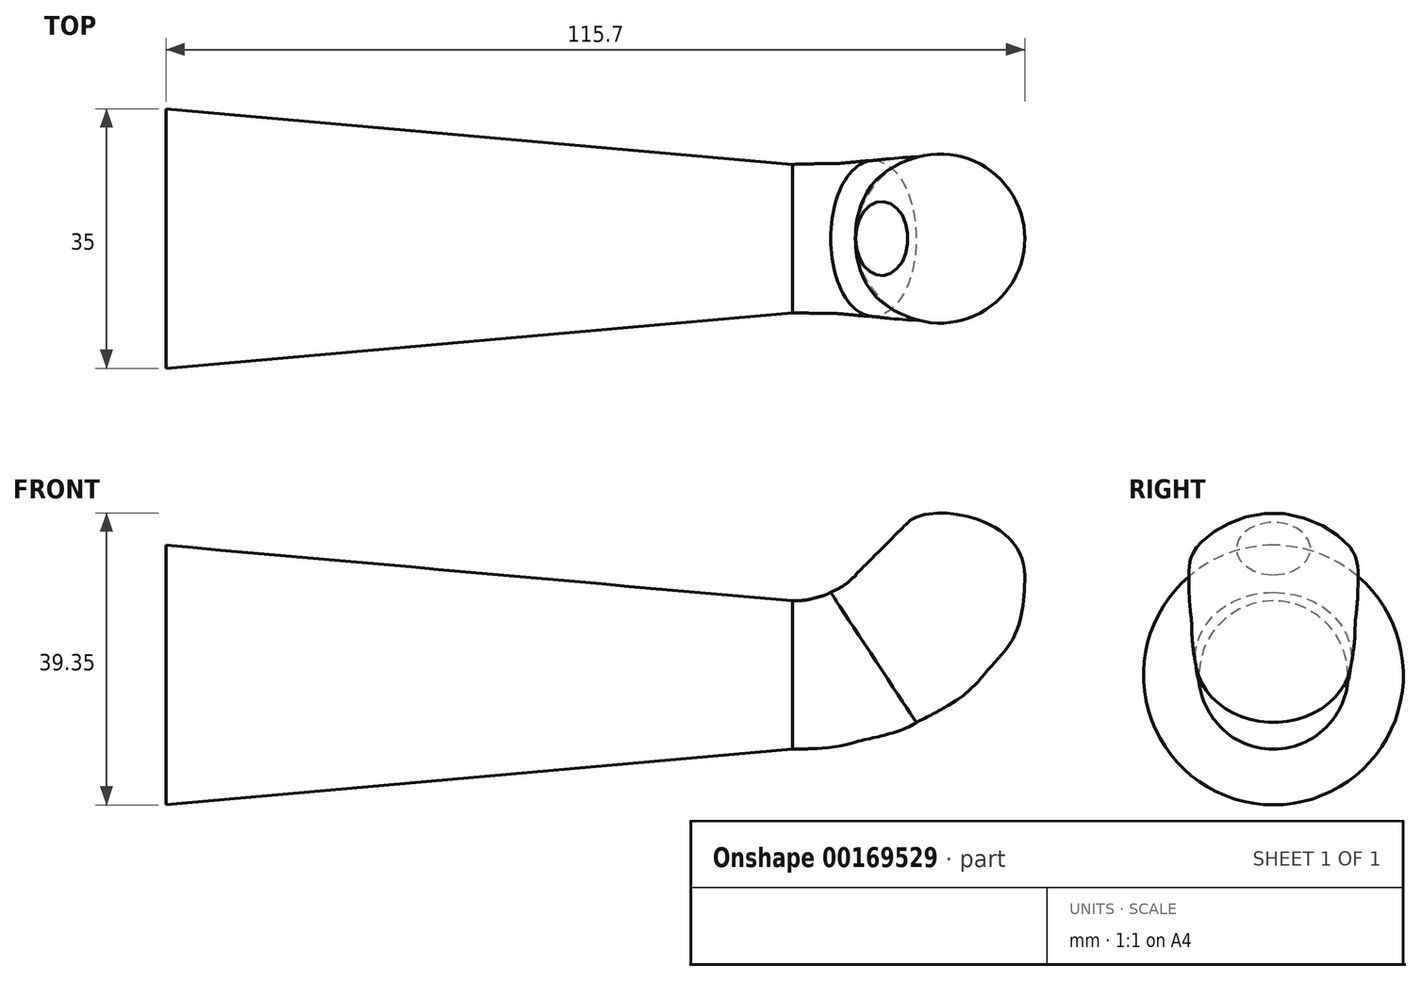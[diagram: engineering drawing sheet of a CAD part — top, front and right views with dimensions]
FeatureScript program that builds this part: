
annotation { "Feature Type Name" : "Feature", "Feature Type Description" : "" }
export const myFeature = defineFeature(function(context is Context, id is Id, definition is map)
    precondition{}
    {
        {
            var Q0;
            Q0=qCreatedBy(makeId("Front.planeOp"),FACE);
            var sketch = newSketch(context, id + "F0", { "sketchPlane" : qUnion([Q0])});
            skLineSegment(sketch, "E0", {"start": v(-55.96, 50) * mm, "end": v(-55.96, -50) * mm});
            skLineSegment(sketch, "E1", {"start": v(36.94, 32.9) * mm, "end": v(47.57, 43.54) * mm});
            skPoint(sketch, "E2", {"position": v(40.5, 36.46) * mm});
            skLineSegment(sketch, "E3", {"start": v(36.96, 32.93) * mm, "end": v(44.04, 40) * mm});
            skPoint(sketch, "E4", {"position": v(-55.96, 9.48) * mm});
            skLineSegment(sketch, "E5", {"start": v(28.46, 29.4) * mm, "end": v(-55.96, 29.4) * mm});
            skPoint(sketch, "E6.visualSharp", {"position": v(33.43, 29.4) * mm});
            skArc(sketch, "E6.filletArc", {"start": v(28.46, 29.4) * mm, "mid": v(33.05, 30.3) * mm, "end": v(36.94, 32.9) * mm});
            skLineSegment(sketch, "E7", {"start": v(28.46, 29.4) * mm, "end": v(28.46, 0) * mm});
            skLineSegment(sketch, "E8", {"start": v(28.46, 21.9) * mm, "end": v(-55.96, 21.9) * mm});
            skSolve(sketch);
        }
        {
            var Q0;
            Q0=sQuery(id+"F0.wireOp",EDGE,"E1");
            extrude(context, id + "F1", {"bodyType" : ToolBodyType.SURFACE, "surfaceEntities" : qUnion([Q0]), "endBound" : BoundingType.SYMMETRIC, "depth" : 15 * mm});
        }
        {
            var Q0;
            Q0=makeQuery(id+"F1.opExtrude","SWEPT_FACE",FACE,{"disambiguationData":[OSD([sQuery(id+"F0.wireOp",EDGE,"E1")])]});
            var sketch = newSketch(context, id + "F2", { "sketchPlane" : qUnion([Q0])});
            skCircle(sketch, "E9", {"center": v(0, 54.4) * mm, "radius": 5 * mm});
            skSolve(sketch);
        }
        {
            var Q0;
            Q0=qCreatedBy(makeId("Front.planeOp"),FACE);
            var sketch = newSketch(context, id + "F3", { "sketchPlane" : qUnion([Q0])});
            skLineSegment(sketch, "E10", {"start": v(28.46, 29.4) * mm, "end": v(28.46, 9.4) * mm});
            skFitSpline(sketch, "E11", {"points": [v(47.48, 43.44) * mm, v(28.46, 9.4) * mm], "startDerivative": vector(67.22, -6.83) * mm, "endDerivative": vector(-97.52, -2.02) * mm});
            skLineSegment(sketch, "E12", {"start": v(36.84, 32.8) * mm, "end": v(59.84, 32.8) * mm});
            skLineSegment(sketch, "E13", {"start": v(36.45, 32.44) * mm, "end": v(53.92, 19.07) * mm});
            skLineSegment(sketch, "E14", {"start": v(33.58, 30.54) * mm, "end": v(45.13, 13) * mm});
            skLineSegment(sketch, "E15", {"start": v(30.98, 29.66) * mm, "end": v(36.61, 10.26) * mm});
            skSolve(sketch);
        }
        {
            var Q0;
            Q0=sQuery(id+"F3.wireOp",EDGE,"E12");
            extrude(context, id + "F4", {"bodyType" : ToolBodyType.SURFACE, "surfaceEntities" : qUnion([Q0]), "endBound" : BoundingType.SYMMETRIC, "depth" : 23 * mm});
        }
        {
            var Q0;
            Q0=sQuery(id+"F3.wireOp",EDGE,"E13");
            extrude(context, id + "F5", {"bodyType" : ToolBodyType.SURFACE, "surfaceEntities" : qUnion([Q0]), "endBound" : BoundingType.SYMMETRIC, "depth" : 22 * mm});
        }
        {
            var Q0;
            Q0=sQuery(id+"F3.wireOp",EDGE,"E14");
            extrude(context, id + "F6", {"bodyType" : ToolBodyType.SURFACE, "surfaceEntities" : qUnion([Q0]), "endBound" : BoundingType.SYMMETRIC, "depth" : 21 * mm});
        }
        {
            var Q0;
            Q0=sQuery(id+"F3.wireOp",EDGE,"E15");
            extrude(context, id + "F7", {"bodyType" : ToolBodyType.SURFACE, "surfaceEntities" : qUnion([Q0]), "endBound" : BoundingType.SYMMETRIC, "depth" : 20.2 * mm});
        }
        {
            var Q0;
            Q0=sQuery(id+"F3.wireOp",EDGE,"E10");
            extrude(context, id + "F8", {"bodyType" : ToolBodyType.SURFACE, "surfaceEntities" : qUnion([Q0]), "endBound" : BoundingType.SYMMETRIC, "depth" : 20 * mm});
        }
        {
            var Q0;
            Q0=makeQuery(id+"F4.opExtrude","SWEPT_FACE",FACE,{"disambiguationData":[OSD([sQuery(id+"F3.wireOp",EDGE,"E12")])]});
            var sketch = newSketch(context, id + "F9", { "sketchPlane" : qUnion([Q0])});
            skPoint(sketch, "E16.centerSnap0", {"position": v(48.34, 11.5) * mm});
            skCircle(sketch, "E17", {"center": v(48.34, 0) * mm, "radius": 11.4 * mm});
            skSolve(sketch);
        }
        {
            var Q0;
            Q0=makeQuery(id+"F5.opExtrude","SWEPT_FACE",FACE,{"disambiguationData":[OSD([sQuery(id+"F3.wireOp",EDGE,"E13")])]});
            var sketch = newSketch(context, id + "F10", { "sketchPlane" : qUnion([Q0])});
            skCircle(sketch, "E18", {"center": v(20.22, 0) * mm, "radius": 11 * mm});
            skPoint(sketch, "E18.centerSnap0", {"position": v(20.22, 11) * mm});
            skSolve(sketch);
        }
        {
            var Q0;
            Q0=makeQuery(id+"F6.opExtrude","SWEPT_FACE",FACE,{"disambiguationData":[OSD([sQuery(id+"F3.wireOp",EDGE,"E14")])]});
            var sketch = newSketch(context, id + "F11", { "sketchPlane" : qUnion([Q0])});
            skCircle(sketch, "E19", {"center": v(0, -3.44) * mm, "radius": 10.5 * mm});
            skPoint(sketch, "E19.centerSnap0", {"position": v(10.5, -3.44) * mm});
            skSolve(sketch);
        }
        {
            var Q0;
            Q0=makeQuery(id+"F7.opExtrude","SWEPT_FACE",FACE,{"disambiguationData":[OSD([sQuery(id+"F3.wireOp",EDGE,"E15")])]});
            var sketch = newSketch(context, id + "F12", { "sketchPlane" : qUnion([Q0])});
            skCircle(sketch, "E20", {"center": v(0, 9.75) * mm, "radius": 10.1 * mm});
            skPoint(sketch, "E20.centerSnap0", {"position": v(10.1, 9.75) * mm});
            skSolve(sketch);
        }
        {
            var Q0;
            Q0=makeQuery(id+"F8.opExtrude","SWEPT_FACE",FACE,{"disambiguationData":[OSD([sQuery(id+"F3.wireOp",EDGE,"E10")])]});
            var sketch = newSketch(context, id + "F13", { "sketchPlane" : qUnion([Q0])});
            skCircle(sketch, "E21", {"center": v(0, 19.4) * mm, "radius": 10 * mm});
            skPoint(sketch, "E21.centerSnap0", {"position": v(10, 19.4) * mm});
            skSolve(sketch);
        }
        {
            var Q0;
            Q0=sQuery(id+"F0.wireOp",EDGE,"E0");
            extrude(context, id + "F14", {"bodyType" : ToolBodyType.SURFACE, "surfaceEntities" : qUnion([Q0]), "endBound" : BoundingType.SYMMETRIC, "depth" : 100 * mm});
        }
        {
            var Q0;
            Q0=makeQuery(id+"F2.imprint","IMPRINT",FACE,{"disambiguationData":[TD([[makeQuery(id+"F2.imprint","IMPRINT",EDGE,{"derivedFrom":sQuery(id+"F2.wireOp",EDGE,"E9")}),1.0]])]});
            var Q1;
            Q1=makeQuery(id+"F9.imprint","IMPRINT",FACE,{"disambiguationData":[TD([[makeQuery(id+"F9.imprint","IMPRINT",EDGE,{"derivedFrom":sQuery(id+"F9.wireOp",EDGE,"E17")}),1.0]])]});
            loft(context, id + "F15", {"startCondition" : LoftEndDerivativeType.TANGENT_TO_PROFILE, "startMagnitude" : 2, "endCondition" : LoftEndDerivativeType.NORMAL_TO_PROFILE, "endMagnitude" : 3, "sheetProfilesArray" : [{ "sheetProfileEntities" : qUnion([Q0]) }, { "sheetProfileEntities" : qUnion([Q1]) }]});
        }
        {
            var Q1;
            Q1=makeQuery(id+"F9.imprint","IMPRINT",FACE,{"disambiguationData":[TD([[makeQuery(id+"F9.imprint","IMPRINT",EDGE,{"derivedFrom":sQuery(id+"F9.wireOp",EDGE,"E17")}),1.0]])]});
            var Q2;
            {var subQ0=sQuery(id+"F10.wireOp",EDGE,"E18");var subQ1=sQuery(id+"F3.wireOp",EDGE,"E13");var subQ2=makeQuery(id+"F10.imprint","INTERSECT",VERTEX,{"derivedFrom":[makeQuery(id+"F5.opExtrude","CAP_EDGE",EDGE,{"disambiguationData":[OSD([subQ1])],"isStart":false}),subQ0]});Q2=makeQuery(id+"F10.imprint","IMPRINT",FACE,{"disambiguationData":[TD([[makeQuery(id+"F10.imprint","IMPRINT",EDGE,{"disambiguationData":[TD([[subQ2,1.0]])],"derivedFrom":subQ0}),1.0]])]});}
            loft(context, id + "F16", {"operationType" : NewBodyOperationType.ADD, "startCondition" : LoftEndDerivativeType.NORMAL_TO_PROFILE, "startMagnitude" : 2, "endCondition" : LoftEndDerivativeType.NORMAL_TO_PROFILE, "endMagnitude" : 1, "sheetProfilesArray" : [{ "sheetProfileEntities" : qUnion([Q1]) }, { "sheetProfileEntities" : qUnion([Q2]) }]});
        }
        {
            var Q1;
            {var subQ0=sQuery(id+"F10.wireOp",EDGE,"E18");var subQ1=sQuery(id+"F3.wireOp",EDGE,"E13");var subQ2=makeQuery(id+"F10.imprint","INTERSECT",VERTEX,{"derivedFrom":[makeQuery(id+"F5.opExtrude","CAP_EDGE",EDGE,{"disambiguationData":[OSD([subQ1])],"isStart":false}),subQ0]});Q1=makeQuery(id+"F10.imprint","IMPRINT",FACE,{"disambiguationData":[TD([[makeQuery(id+"F10.imprint","IMPRINT",EDGE,{"disambiguationData":[TD([[subQ2,1.0]])],"derivedFrom":subQ0}),1.0]])]});}
            var Q2;
            {var subQ0=sQuery(id+"F11.wireOp",EDGE,"E19");var subQ1=makeQuery(id+"F11.imprint","INTERSECT",VERTEX,{"derivedFrom":[makeQuery(id+"F6.opExtrude","SWEPT_EDGE",EDGE,{"disambiguationData":[OSD([sQuery(id+"F3.wireOp",VERTEX,"E14.start")])]}),subQ0]});Q2=makeQuery(id+"F11.imprint","IMPRINT",FACE,{"disambiguationData":[TD([[makeQuery(id+"F11.imprint","IMPRINT",EDGE,{"disambiguationData":[TD([[subQ1,1.0]])],"derivedFrom":subQ0}),1.0]])]});}
            loft(context, id + "F17", {"operationType" : NewBodyOperationType.ADD, "startCondition" : LoftEndDerivativeType.NORMAL_TO_PROFILE, "startMagnitude" : 1, "sheetProfilesArray" : [{ "sheetProfileEntities" : qUnion([Q1]) }, { "sheetProfileEntities" : qUnion([Q2]) }]});
        }
        {
            var Q1;
            {var subQ0=sQuery(id+"F11.wireOp",EDGE,"E19");var subQ1=makeQuery(id+"F11.imprint","INTERSECT",VERTEX,{"derivedFrom":[makeQuery(id+"F6.opExtrude","SWEPT_EDGE",EDGE,{"disambiguationData":[OSD([sQuery(id+"F3.wireOp",VERTEX,"E14.start")])]}),subQ0]});Q1=makeQuery(id+"F11.imprint","IMPRINT",FACE,{"disambiguationData":[TD([[makeQuery(id+"F11.imprint","IMPRINT",EDGE,{"disambiguationData":[TD([[subQ1,1.0]])],"derivedFrom":subQ0}),1.0]])]});}
            var Q2;
            {var subQ0=sQuery(id+"F12.wireOp",EDGE,"E20");var subQ1=makeQuery(id+"F12.imprint","INTERSECT",VERTEX,{"derivedFrom":[makeQuery(id+"F7.opExtrude","SWEPT_EDGE",EDGE,{"disambiguationData":[OSD([sQuery(id+"F3.wireOp",VERTEX,"E15.start")])]}),subQ0]});Q2=makeQuery(id+"F12.imprint","IMPRINT",FACE,{"disambiguationData":[TD([[makeQuery(id+"F12.imprint","IMPRINT",EDGE,{"disambiguationData":[TD([[subQ1,1.0]])],"derivedFrom":subQ0}),1.0]])]});}
            loft(context, id + "F18", {"operationType" : NewBodyOperationType.ADD, "startCondition" : LoftEndDerivativeType.NORMAL_TO_PROFILE, "startMagnitude" : 1, "endCondition" : LoftEndDerivativeType.NORMAL_TO_PROFILE, "endMagnitude" : 1, "sheetProfilesArray" : [{ "sheetProfileEntities" : qUnion([Q1]) }, { "sheetProfileEntities" : qUnion([Q2]) }]});
        }
        {
            var Q1;
            {var subQ0=sQuery(id+"F12.wireOp",EDGE,"E20");var subQ1=makeQuery(id+"F12.imprint","INTERSECT",VERTEX,{"derivedFrom":[makeQuery(id+"F7.opExtrude","SWEPT_EDGE",EDGE,{"disambiguationData":[OSD([sQuery(id+"F3.wireOp",VERTEX,"E15.start")])]}),subQ0]});Q1=makeQuery(id+"F12.imprint","IMPRINT",FACE,{"disambiguationData":[TD([[makeQuery(id+"F12.imprint","IMPRINT",EDGE,{"disambiguationData":[TD([[subQ1,1.0]])],"derivedFrom":subQ0}),1.0]])]});}
            var Q2;
            {var subQ0=sQuery(id+"F13.wireOp",EDGE,"E21");var subQ1=makeQuery(id+"F13.imprint","INTERSECT",VERTEX,{"derivedFrom":[makeQuery(id+"F8.opExtrude","SWEPT_EDGE",EDGE,{"disambiguationData":[OSD([sQuery(id+"F3.wireOp",VERTEX,"E10.start")])]}),subQ0]});Q2=makeQuery(id+"F13.imprint","IMPRINT",FACE,{"disambiguationData":[TD([[makeQuery(id+"F13.imprint","IMPRINT",EDGE,{"disambiguationData":[TD([[subQ1,1.0]])],"derivedFrom":subQ0}),1.0]])]});}
            loft(context, id + "F19", {"operationType" : NewBodyOperationType.ADD, "startCondition" : LoftEndDerivativeType.NORMAL_TO_PROFILE, "startMagnitude" : 1, "sheetProfilesArray" : [{ "sheetProfileEntities" : qUnion([Q1]) }, { "sheetProfileEntities" : qUnion([Q2]) }]});
        }
        {
            var Q0;
            Q0=qCreatedBy(makeId("Front.planeOp"),FACE);
            var sketch = newSketch(context, id + "F20", { "sketchPlane" : qUnion([Q0])});
            skPoint(sketch, "E22", {"position": v(28.46, 19.4) * mm});
            skLineSegment(sketch, "E23", {"start": v(28.46, 19.4) * mm, "end": v(-55.96, 19.4) * mm});
            skSolve(sketch);
        }
        {
            var Q0;
            Q0=makeQuery(id+"F14.opExtrude","SWEPT_FACE",FACE,{"disambiguationData":[OSD([sQuery(id+"F0.wireOp",EDGE,"E0")])]});
            var sketch = newSketch(context, id + "F21", { "sketchPlane" : qUnion([Q0])});
            skCircle(sketch, "E24", {"center": v(0, 19.4) * mm, "radius": 17.5 * mm});
            skSolve(sketch);
        }
        {
            var Q1;
            {var subQ0=sQuery(id+"F13.wireOp",EDGE,"E21");var subQ1=makeQuery(id+"F13.imprint","INTERSECT",VERTEX,{"derivedFrom":[makeQuery(id+"F8.opExtrude","SWEPT_EDGE",EDGE,{"disambiguationData":[OSD([sQuery(id+"F3.wireOp",VERTEX,"E10.start")])]}),subQ0]});Q1=makeQuery(id+"F13.imprint","IMPRINT",FACE,{"disambiguationData":[TD([[makeQuery(id+"F13.imprint","IMPRINT",EDGE,{"disambiguationData":[TD([[subQ1,1.0]])],"derivedFrom":subQ0}),1.0]])]});}
            var Q2;
            Q2=makeQuery(id+"F21.imprint","IMPRINT",FACE,{"disambiguationData":[TD([[makeQuery(id+"F21.imprint","IMPRINT",EDGE,{"derivedFrom":sQuery(id+"F21.wireOp",EDGE,"E24")}),1.0]])]});
            loft(context, id + "F22", {"operationType" : NewBodyOperationType.ADD, "sheetProfilesArray" : [{ "sheetProfileEntities" : qUnion([Q1]) }, { "sheetProfileEntities" : qUnion([Q2]) }]});
        }
    });
